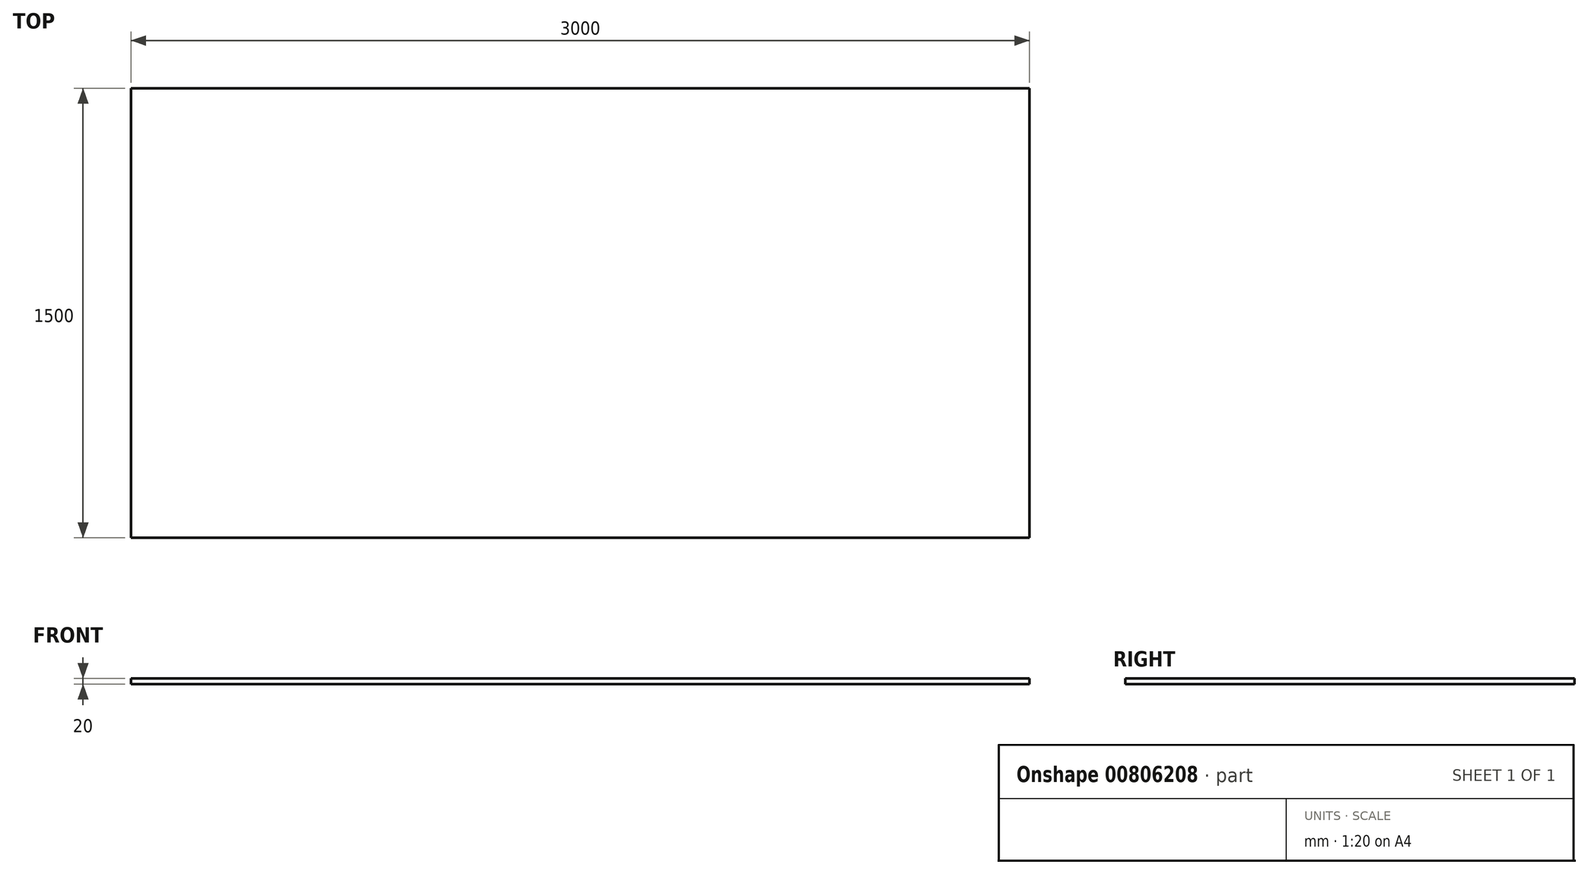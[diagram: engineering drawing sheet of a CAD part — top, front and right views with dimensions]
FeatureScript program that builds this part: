
annotation { "Feature Type Name" : "Feature", "Feature Type Description" : "" }
export const myFeature = defineFeature(function(context is Context, id is Id, definition is map)
    precondition{}
    {
        {
            var Q0;
            Q0=qCreatedBy(makeId("Top.planeOp"),FACE);
            var sketch = newSketch(context, id + "F0", { "sketchPlane" : qUnion([Q0])});
            skLineSegment(sketch, "E0.bottom", {"start": v(1500, -750) * mm, "end": v(-1500, -750) * mm});
            skLineSegment(sketch, "E0.top", {"start": v(1500, 750) * mm, "end": v(-1500, 750) * mm});
            skLineSegment(sketch, "E0.left", {"start": v(1500, -750) * mm, "end": v(1500, 750) * mm});
            skLineSegment(sketch, "E0.right", {"start": v(-1500, -750) * mm, "end": v(-1500, 750) * mm});
            skPoint(sketch, "E0.middle", {"position": v(0, 0) * mm});
            skSolve(sketch);
        }
        {
            var Q0;
            Q0=makeQuery(id+"F0.imprint","IMPRINT",FACE,{"disambiguationData":[TD([[makeQuery(id+"F0.imprint","IMPRINT",EDGE,{"derivedFrom":sQuery(id+"F0.wireOp",EDGE,"E0.bottom")}),-1.0]])]});
            extrude(context, id + "F1", {"entities" : qUnion([Q0]), "depth" : 20 * mm, "offsetDistance" : 25 * mm});
        }
    });
